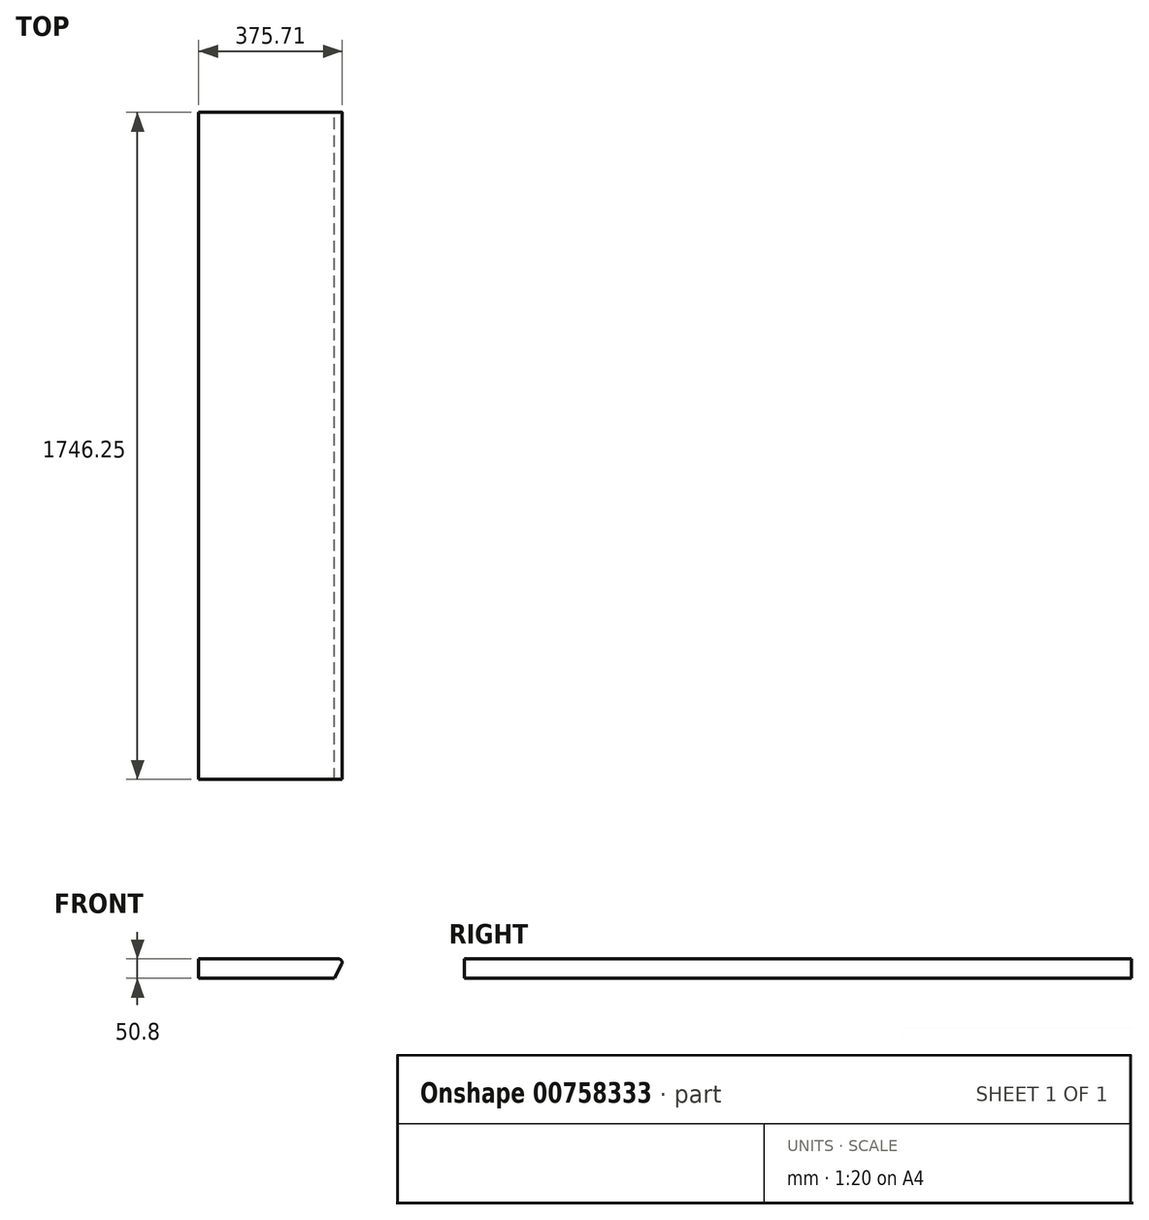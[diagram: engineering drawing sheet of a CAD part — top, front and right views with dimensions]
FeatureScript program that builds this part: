
annotation { "Feature Type Name" : "Feature", "Feature Type Description" : "" }
export const myFeature = defineFeature(function(context is Context, id is Id, definition is map)
    precondition{}
    {
        {
            var Q0;
            Q0=qCreatedBy(makeId("Front.planeOp"),FACE);
            var sketch = newSketch(context, id + "F0", { "sketchPlane" : qUnion([Q0])});
            skLineSegment(sketch, "E0", {"start": v(-258.93, 0) * mm, "end": v(-258.93, 50.8) * mm});
            skLineSegment(sketch, "E1", {"start": v(-258.93, 50.8) * mm, "end": v(107.26, 50.8) * mm});
            skLineSegment(sketch, "E2", {"start": v(115.72, 36.9) * mm, "end": v(96.67, 0) * mm});
            skLineSegment(sketch, "E3", {"start": v(96.67, 0) * mm, "end": v(-258.93, 0) * mm});
            skArc(sketch, "E4.filletArc", {"start": v(115.72, 36.9) * mm, "mid": v(115.4, 46.23) * mm, "end": v(107.26, 50.8) * mm});
            skSolve(sketch);
        }
        {
            var Q0;
            Q0 = qSketchRegion(id + "F0", true);
            extrude(context, id + "F1", {"entities" : qUnion([Q0]), "depth" : 1746.25 * mm, "offsetDistance" : 25.4 * mm});
        }
    });
